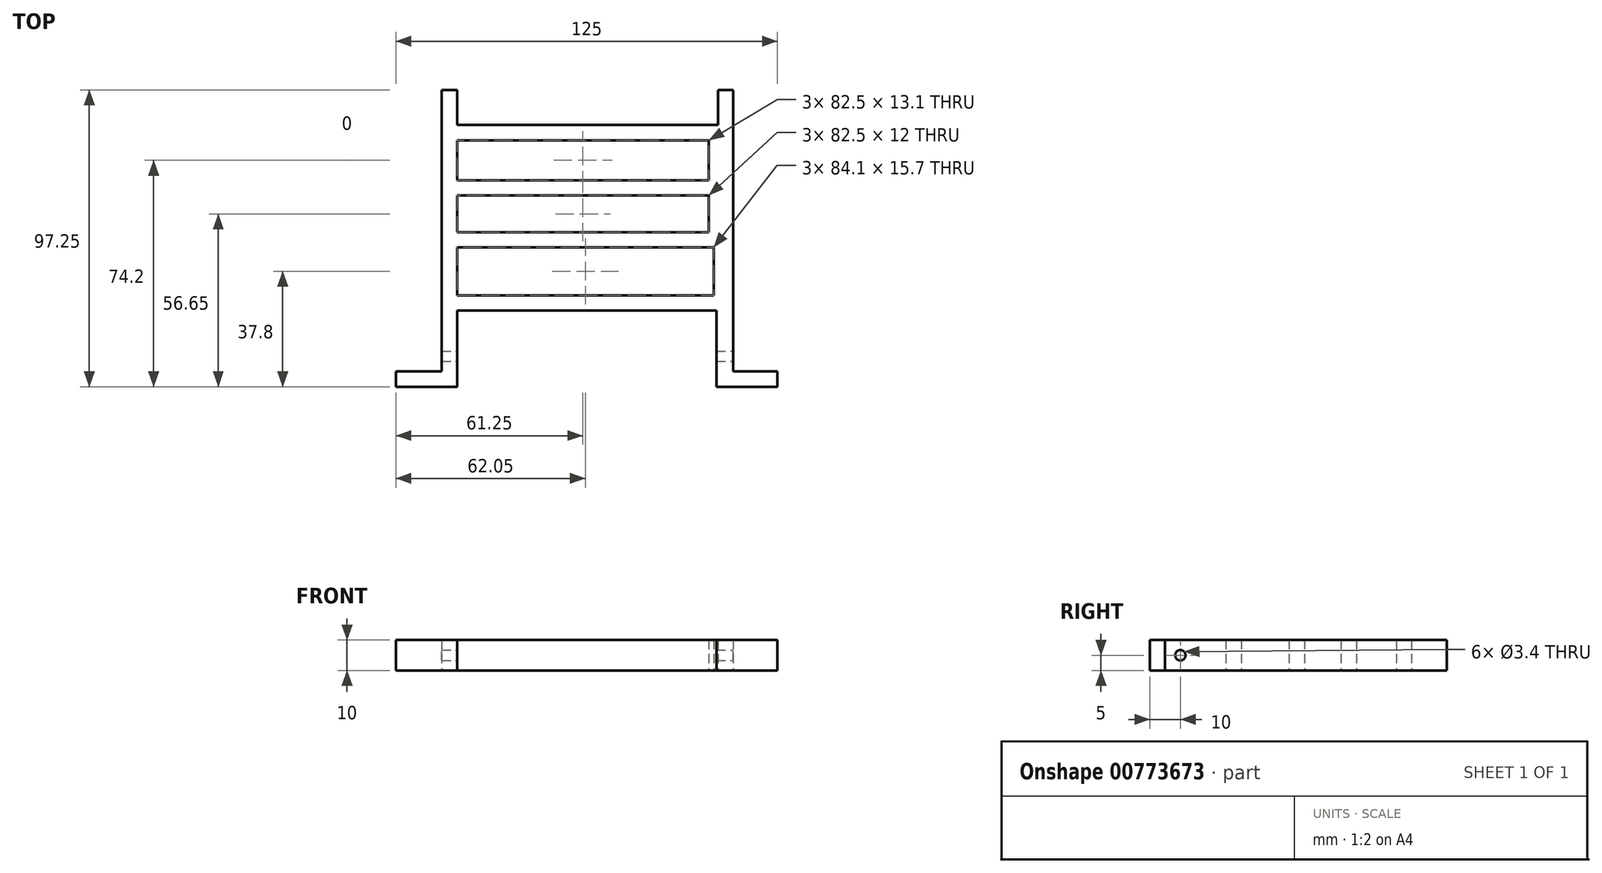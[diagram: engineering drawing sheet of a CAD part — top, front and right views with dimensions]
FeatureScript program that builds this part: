
annotation { "Feature Type Name" : "Feature", "Feature Type Description" : "" }
export const myFeature = defineFeature(function(context is Context, id is Id, definition is map)
    precondition{}
    {
        {
            var Q0;
            Q0=qCreatedBy(makeId("Top.planeOp"),FACE);
            var sketch = newSketch(context, id + "F0", { "sketchPlane" : qUnion([Q0])});
            skLineSegment(sketch, "E0.bottom", {"start": v(0, 0) * mm, "end": v(82.5, 0) * mm});
            skLineSegment(sketch, "E0.top", {"start": v(0, -13.1) * mm, "end": v(82.5, -13.1) * mm});
            skLineSegment(sketch, "E0.left", {"start": v(0, 0) * mm, "end": v(0, -13.1) * mm});
            skLineSegment(sketch, "E0.right", {"start": v(82.5, 0) * mm, "end": v(82.5, -13.1) * mm});
            skLineSegment(sketch, "E1.bottom", {"start": v(0, -18.1) * mm, "end": v(82.5, -18.1) * mm});
            skLineSegment(sketch, "E1.top", {"start": v(0, -30.1) * mm, "end": v(82.5, -30.1) * mm});
            skLineSegment(sketch, "E1.left", {"start": v(0, -18.1) * mm, "end": v(0, -30.1) * mm});
            skLineSegment(sketch, "E1.right", {"start": v(82.5, -18.1) * mm, "end": v(82.5, -30.1) * mm});
            skLineSegment(sketch, "E2.bottom", {"start": v(0, -35.1) * mm, "end": v(84.1, -35.1) * mm});
            skLineSegment(sketch, "E2.top", {"start": v(0, -50.8) * mm, "end": v(84.1, -50.8) * mm});
            skLineSegment(sketch, "E2.left", {"start": v(0, -35.1) * mm, "end": v(0, -50.8) * mm});
            skLineSegment(sketch, "E2.right", {"start": v(84.1, -35.1) * mm, "end": v(84.1, -50.8) * mm});
            skLineSegment(sketch, "E3.bottom", {"start": v(0, 5) * mm, "end": v(85.5, 5) * mm});
            skLineSegment(sketch, "E3.left", {"start": v(0, 5) * mm, "end": v(0, 16.5) * mm});
            skLineSegment(sketch, "E3.right", {"start": v(85.5, 5) * mm, "end": v(85.5, 16.5) * mm});
            skLineSegment(sketch, "E4", {"start": v(-5, 16.5) * mm, "end": v(-5, -75.75) * mm});
            skLineSegment(sketch, "E5", {"start": v(-5, 16.5) * mm, "end": v(0, 16.5) * mm});
            skLineSegment(sketch, "E6", {"start": v(85.5, 16.5) * mm, "end": v(90.5, 16.5) * mm});
            skLineSegment(sketch, "E7", {"start": v(90.5, 16.5) * mm, "end": v(90.5, -75.75) * mm});
            skLineSegment(sketch, "E8.bottom", {"start": v(0, -55.8) * mm, "end": v(85, -55.8) * mm});
            skLineSegment(sketch, "E8.left", {"start": v(0, -55.8) * mm, "end": v(0, -80.75) * mm});
            skLineSegment(sketch, "E8.right", {"start": v(85, -55.8) * mm, "end": v(85, -80.75) * mm});
            skLineSegment(sketch, "E9.bottom", {"start": v(0, -80.75) * mm, "end": v(-20, -80.75) * mm});
            skLineSegment(sketch, "E9.top", {"start": v(-5, -75.75) * mm, "end": v(-20, -75.75) * mm});
            skLineSegment(sketch, "E9.left", {"start": v(0, -80.75) * mm, "end": v(0, -75.75) * mm});
            skLineSegment(sketch, "E9.right", {"start": v(-20, -80.75) * mm, "end": v(-20, -75.75) * mm});
            skLineSegment(sketch, "E10.bottom", {"start": v(85, -80.75) * mm, "end": v(105, -80.75) * mm});
            skLineSegment(sketch, "E10.top", {"start": v(90.5, -75.75) * mm, "end": v(105, -75.75) * mm});
            skLineSegment(sketch, "E10.left", {"start": v(85, -80.75) * mm, "end": v(85, -75.75) * mm});
            skLineSegment(sketch, "E10.right", {"start": v(105, -80.75) * mm, "end": v(105, -75.75) * mm});
            skLineSegment(sketch, "E11.trimOffspring", {"start": v(-5, -80.75) * mm, "end": v(-5, -80.8) * mm});
            skLineSegment(sketch, "E12.trimOffspring", {"start": v(90.5, -80.75) * mm, "end": v(90.5, -80.8) * mm});
            skSolve(sketch);
        }
        {
            var Q0;
            Q0 = qSketchRegion(id + "F0", true);
            extrude(context, id + "F1", {"entities" : qUnion([Q0]), "depth" : 10 * mm, "offsetDistance" : 25 * mm});
        }
        {
            var Q0;
            Q0=makeQuery(id+"F1.opExtrude","SWEPT_FACE",FACE,{"disambiguationData":[OSD([sQuery(id+"F0.wireOp",EDGE,"E7")])]});
            var sketch = newSketch(context, id + "F2", { "sketchPlane" : qUnion([Q0])});
            skCircle(sketch, "E13", {"center": v(-70.75, 5) * mm, "radius": 1.7 * mm});
            skSolve(sketch);
        }
        {
            var Q0;
            Q0 = qSketchRegion(id + "F2", true);
            extrude(context, id + "F3", {"entities" : qUnion([Q0]), "operationType" : NewBodyOperationType.REMOVE, "endBound" : BoundingType.THROUGH_ALL, "oppositeDirection" : true, "depth" : 25 * mm, "offsetDistance" : 25 * mm});
        }
    });
